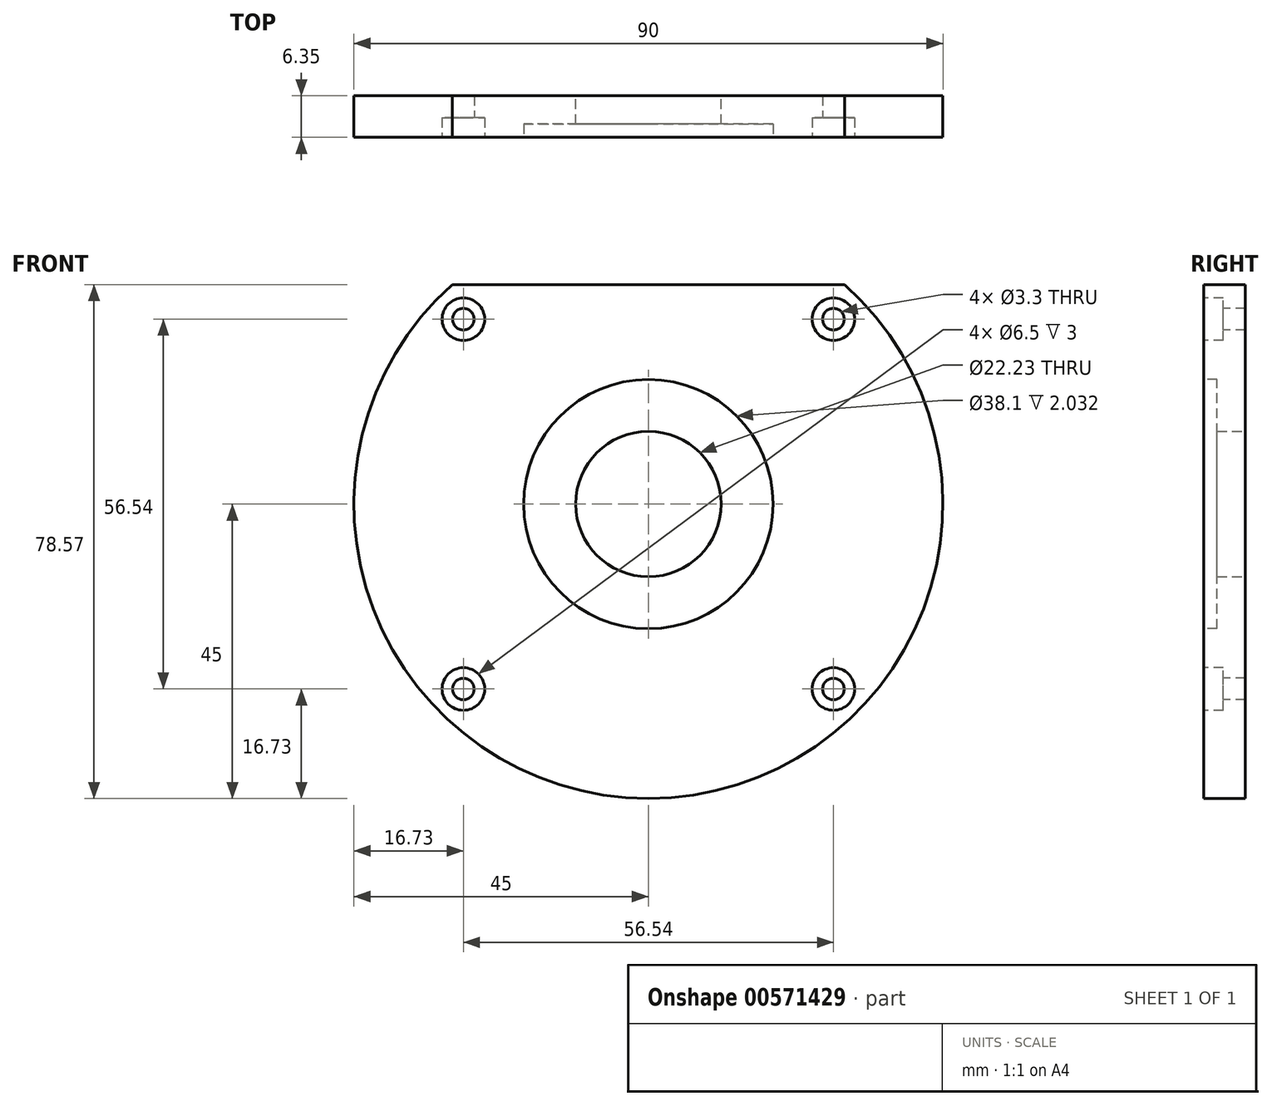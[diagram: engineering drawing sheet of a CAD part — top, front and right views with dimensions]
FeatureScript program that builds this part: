
annotation { "Feature Type Name" : "Feature", "Feature Type Description" : "" }
export const myFeature = defineFeature(function(context is Context, id is Id, definition is map)
    precondition{}
    {
        {
            var Q0;
            Q0=qCreatedBy(makeId("Front.planeOp"),FACE);
            var sketch = newSketch(context, id + "F0", { "sketchPlane" : qUnion([Q0])});
            skCircle(sketch, "E0", {"center": v(0, 0) * mm, "radius": 45 * mm});
            skCircle(sketch, "E1", {"center": v(0, 0) * mm, "radius": 11.11 * mm});
            skSolve(sketch);
        }
        {
            var Q0;
            Q0 = qSketchRegion(id + "F0", true);
            extrude(context, id + "F1", {"entities" : qUnion([Q0]), "depth" : 6.35 * mm, "offsetDistance" : 25.4 * mm});
        }
        {
            var Q0;
            Q0=makeQuery(id+"F1.opExtrude","CAP_FACE",FACE,{"disambiguationData":[OSD([sQuery(id+"F0.wireOp",EDGE,"E0"),sQuery(id+"F0.wireOp",EDGE,"E1")])],"isStart":false});
            var sketch = newSketch(context, id + "F2", { "sketchPlane" : qUnion([Q0])});
            skCircle(sketch, "E2", {"center": v(0, 0) * mm, "radius": 19.05 * mm});
            skSolve(sketch);
        }
        {
            var Q0;
            Q0 = qSketchRegion(id + "F2", true);
            extrude(context, id + "F3", {"entities" : qUnion([Q0]), "operationType" : NewBodyOperationType.REMOVE, "oppositeDirection" : true, "depth" : 2.03 * mm, "offsetDistance" : 25.4 * mm});
        }
        {
            var Q0;
            Q0=makeQuery(id+"F1.opExtrude","CAP_FACE",FACE,{"disambiguationData":[OSD([sQuery(id+"F0.wireOp",EDGE,"E0"),sQuery(id+"F0.wireOp",EDGE,"E1")])],"isStart":false});
            var sketch = newSketch(context, id + "F4", { "sketchPlane" : qUnion([Q0])});
            skPoint(sketch, "E3", {"position": v(-28.27, 28.27) * mm});
            skPoint(sketch, "E4", {"position": v(28.27, 28.27) * mm});
            skPoint(sketch, "E5", {"position": v(28.27, -28.27) * mm});
            skPoint(sketch, "E6", {"position": v(-28.27, -28.27) * mm});
            skSolve(sketch);
        }
        {
            var Q0;
            Q0=sQuery(id+"F4.wireOp",VERTEX,"E3");
            var Q1;
            Q1=sQuery(id+"F4.wireOp",VERTEX,"E4");
            var Q2;
            Q2=sQuery(id+"F4.wireOp",VERTEX,"E5");
            var Q3;
            Q3=sQuery(id+"F4.wireOp",VERTEX,"E6");
            var Q4;
            Q4=makeQuery(id+"F1.opExtrude","SWEPT_BODY",BODY,{"disambiguationData":[OSD([sQuery(id+"F0.wireOp",EDGE,"E0"),sQuery(id+"F0.wireOp",EDGE,"E1")])]});
            hole(context, id + "F5", {"style" : HoleStyle.C_BORE, "endStyle" : HoleEndStyle.THROUGH, "standardTappedOrClearance" : lookupTablePath({ "standard" : "ISO", "fit" : "Normal", "size" : "M3", "type" : "Clearance" }), "standardBlindInLast" : lookupTablePath({ "fit" : "Standard", "standard" : "ISO", "size" : "M3", "type" : "Clearance" }), "holeDiameter" : 3.3 * mm, "cBoreDiameter" : 6.5 * mm, "cBoreDepth" : 3 * mm, "isTappedThrough" : true, "tappedDepth" : 8.9 * mm, "tapClearance" : 1, "locations" : qUnion([Q0, Q1, Q2, Q3]), "scope" : qUnion([Q4])});
        }
        {
            var Q0;
            Q0=makeQuery(id+"F1.opExtrude","CAP_FACE",FACE,{"disambiguationData":[OSD([sQuery(id+"F0.wireOp",EDGE,"E0"),sQuery(id+"F0.wireOp",EDGE,"E1")])],"isStart":false});
            var sketch = newSketch(context, id + "F6", { "sketchPlane" : qUnion([Q0])});
            skLineSegment(sketch, "E7", {"start": v(-29.97, 33.57) * mm, "end": v(29.97, 33.57) * mm});
            skArc(sketch, "E8", {"start": v(-29.97, 33.57) * mm, "mid": v(0, 45) * mm, "end": v(29.97, 33.57) * mm});
            skSolve(sketch);
        }
        {
            var Q0;
            Q0 = qSketchRegion(id + "F6", true);
            extrude(context, id + "F7", {"entities" : qUnion([Q0]), "operationType" : NewBodyOperationType.REMOVE, "oppositeDirection" : true, "depth" : 25.4 * mm, "offsetDistance" : 25.4 * mm});
        }
    });
